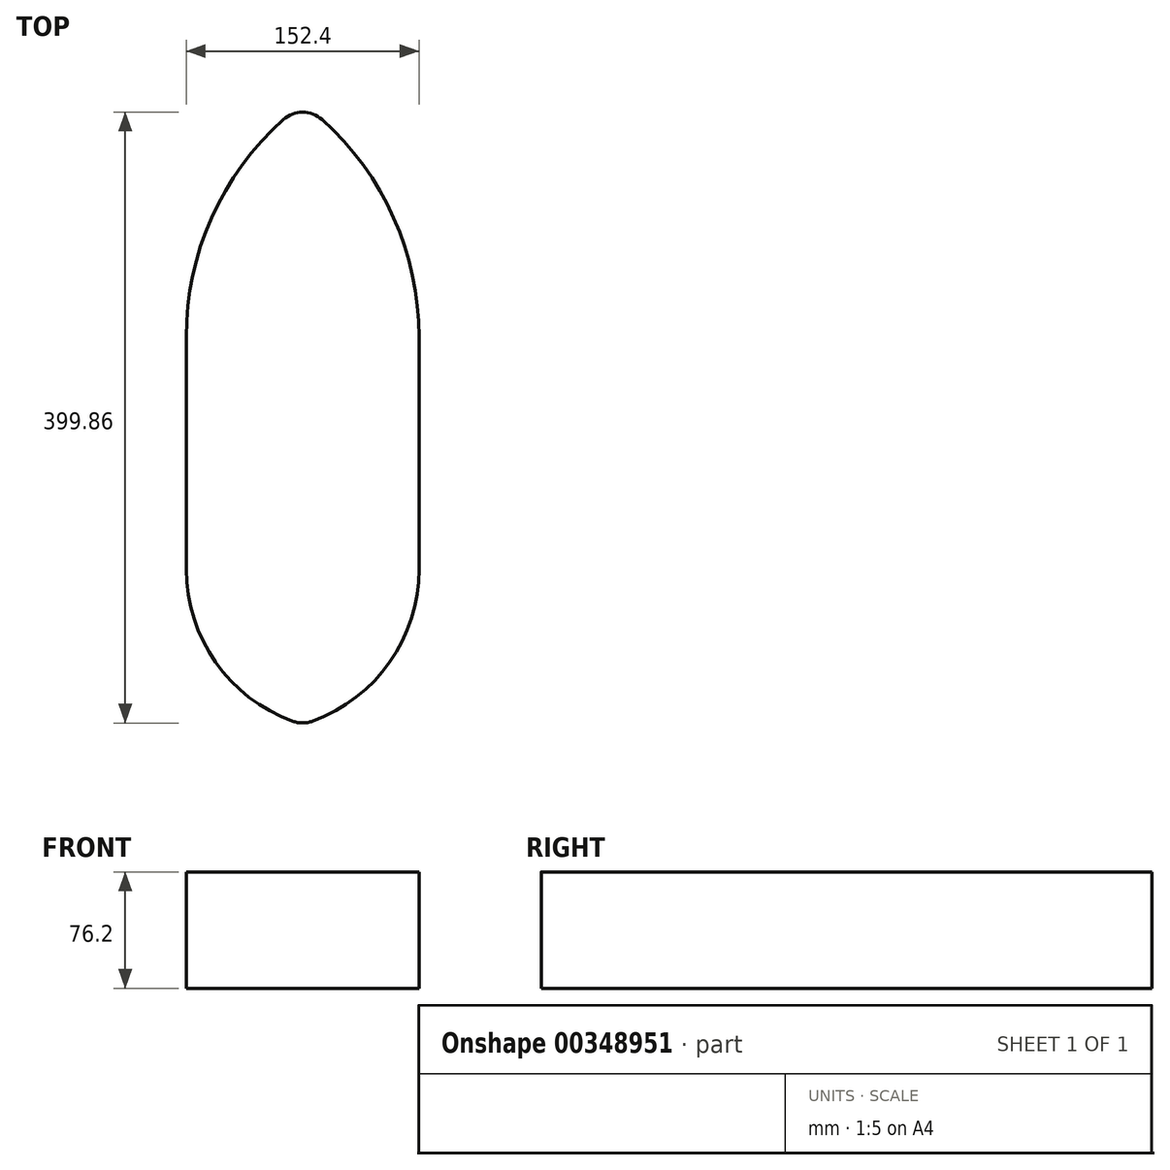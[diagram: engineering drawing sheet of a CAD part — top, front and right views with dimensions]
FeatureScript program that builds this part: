
annotation { "Feature Type Name" : "Feature", "Feature Type Description" : "" }
export const myFeature = defineFeature(function(context is Context, id is Id, definition is map)
    precondition{}
    {
        {
            var Q0;
            Q0=qCreatedBy(makeId("Top.planeOp"),FACE);
            var sketch = newSketch(context, id + "F0", { "sketchPlane" : qUnion([Q0])});
            skLineSegment(sketch, "E0", {"start": v(0, 0) * mm, "end": v(-76.2, 0) * mm, "construction": true});
            skLineSegment(sketch, "E1", {"start": v(0, 0) * mm, "end": v(76.2, 0) * mm, "construction": true});
            skLineSegment(sketch, "E2", {"start": v(-76.2, 76.2) * mm, "end": v(-76.2, -76.2) * mm});
            skLineSegment(sketch, "E3", {"start": v(76.2, 76.2) * mm, "end": v(76.2, -76.2) * mm});
            skLineSegment(sketch, "E4", {"start": v(-76.2, -76.2) * mm, "end": v(0, -76.2) * mm, "construction": true});
            skLineSegment(sketch, "E5", {"start": v(0, -76.2) * mm, "end": v(76.2, -76.2) * mm, "construction": true});
            skLineSegment(sketch, "E6", {"start": v(0, 76.2) * mm, "end": v(-76.2, 76.2) * mm, "construction": true});
            skLineSegment(sketch, "E7", {"start": v(0, 76.2) * mm, "end": v(76.2, 76.2) * mm, "construction": true});
            skLineSegment(sketch, "E8", {"start": v(0, 76.2) * mm, "end": v(0, -76.2) * mm, "construction": true});
            skLineSegment(sketch, "E9", {"start": v(0, -76.2) * mm, "end": v(0, -177.8) * mm, "construction": true});
            skArc(sketch, "E10", {"start": v(-76.2, -76.2) * mm, "mid": v(-57.04, -136.93) * mm, "end": v(-6.5, -175.67) * mm});
            skArc(sketch, "E11.MirrorCS", {"start": v(76.2, -76.2) * mm, "mid": v(57.04, -136.93) * mm, "end": v(6.5, -175.67) * mm});
            skPoint(sketch, "E12.visualSharp", {"position": v(0, -177.8) * mm});
            skArc(sketch, "E12.filletArc", {"start": v(-6.5, -175.67) * mm, "mid": v(0, -176.82) * mm, "end": v(6.5, -175.67) * mm});
            skLineSegment(sketch, "E13", {"start": v(0, 76.2) * mm, "end": v(0, 228.6) * mm, "construction": true});
            skArc(sketch, "E14", {"start": v(-12.7, 218.2) * mm, "mid": v(-59.6, 153.97) * mm, "end": v(-76.2, 76.2) * mm});
            skArc(sketch, "E15.MirrorCS", {"start": v(12.7, 218.2) * mm, "mid": v(59.6, 153.97) * mm, "end": v(76.2, 76.2) * mm});
            skPoint(sketch, "E16.visualSharp", {"position": v(0, 228.6) * mm});
            skArc(sketch, "E16.filletArc", {"start": v(12.7, 218.2) * mm, "mid": v(0, 223.04) * mm, "end": v(-12.7, 218.2) * mm});
            skLineSegment(sketch, "E17", {"start": v(0, 185.63) * mm, "end": v(76.2, 185.63) * mm, "construction": true});
            skLineSegment(sketch, "E18", {"start": v(12.7, 218.2) * mm, "end": v(12.7, 185.63) * mm, "construction": true});
            skLineSegment(sketch, "E19", {"start": v(12.7, 185.63) * mm, "end": v(12.7, 76.2) * mm, "construction": true});
            skLineSegment(sketch, "E20.MirrorCS", {"start": v(0, 185.63) * mm, "end": v(-76.2, 185.63) * mm, "construction": true});
            skLineSegment(sketch, "E21.MirrorCS", {"start": v(-12.7, 185.63) * mm, "end": v(-12.7, 76.2) * mm, "construction": true});
            skLineSegment(sketch, "E22.MirrorCS", {"start": v(-12.7, 218.2) * mm, "end": v(-12.7, 185.63) * mm, "construction": true});
            skArc(sketch, "E23", {"start": v(69.4, 180.76) * mm, "mid": v(61.51, 170.86) * mm, "end": v(57.3, 158.92) * mm});
            skLineSegment(sketch, "E24", {"start": v(82.12, 185.63) * mm, "end": v(222.66, 185.63) * mm});
            skArc(sketch, "E25", {"start": v(152.22, 152.4) * mm, "mid": v(98.45, 130.02) * mm, "end": v(76.2, 76.2) * mm});
            skLineSegment(sketch, "E26", {"start": v(152.25, 152.4) * mm, "end": v(203.2, 152.4) * mm});
            skPoint(sketch, "E27.visualSharp", {"position": v(76.2, 185.63) * mm});
            skArc(sketch, "E27.filletArc", {"start": v(82.12, 185.63) * mm, "mid": v(75.3, 184.37) * mm, "end": v(69.4, 180.76) * mm});
            skPoint(sketch, "E28.visualSharp", {"position": v(152.57, 152.4) * mm});
            skArc(sketch, "E28.filletArc", {"start": v(152.25, 152.4) * mm, "mid": v(152.23, 152.4) * mm, "end": v(152.22, 152.4) * mm});
            skCircle(sketch, "E29", {"center": v(241.3, 152.4) * mm, "radius": 38.1 * mm});
            skLineSegment(sketch, "E30", {"start": v(203.2, 152.4) * mm, "end": v(203.2, 0) * mm, "construction": true});
            skLineSegment(sketch, "E31", {"start": v(203.2, 0) * mm, "end": v(76.2, 0) * mm, "construction": true});
            skLineSegment(sketch, "E32", {"start": v(76.2, 76.2) * mm, "end": v(203.2, 76.2) * mm, "construction": true});
            skLineSegment(sketch, "E33", {"start": v(152.57, 152.4) * mm, "end": v(60.2, 152.6) * mm, "construction": true});
            skLineSegment(sketch, "E34", {"start": v(241.3, 152.4) * mm, "end": v(203.2, 152.4) * mm, "construction": true});
            skArc(sketch, "E35.MirrorCS", {"start": v(-152.22, 152.4) * mm, "mid": v(-98.45, 130.02) * mm, "end": v(-76.2, 76.2) * mm});
            skLineSegment(sketch, "E36.MirrorCS", {"start": v(-152.57, 152.4) * mm, "end": v(-60.2, 152.6) * mm, "construction": true});
            skLineSegment(sketch, "E37.MirrorCS", {"start": v(-152.25, 152.4) * mm, "end": v(-203.2, 152.4) * mm});
            skLineSegment(sketch, "E38.MirrorCS", {"start": v(-241.3, 152.4) * mm, "end": v(-203.2, 152.4) * mm, "construction": true});
            skCircle(sketch, "E39.MirrorC", {"center": v(-241.3, 152.4) * mm, "radius": 38.1 * mm});
            skLineSegment(sketch, "E40.MirrorCS", {"start": v(-82.12, 185.63) * mm, "end": v(-222.66, 185.63) * mm});
            skArc(sketch, "E41.MirrorCS", {"start": v(-82.12, 185.63) * mm, "mid": v(-75.3, 184.37) * mm, "end": v(-69.4, 180.76) * mm});
            skArc(sketch, "E42.MirrorCS", {"start": v(-69.4, 180.76) * mm, "mid": v(-61.51, 170.86) * mm, "end": v(-57.3, 158.92) * mm});
            skArc(sketch, "E43.MirrorCS", {"start": v(152.22, -152.4) * mm, "mid": v(98.45, -130.02) * mm, "end": v(76.2, -76.2) * mm});
            skLineSegment(sketch, "E44.MirrorCS", {"start": v(152.25, -152.4) * mm, "end": v(203.2, -152.4) * mm});
            skLineSegment(sketch, "E45.MirrorCS", {"start": v(82.12, -185.63) * mm, "end": v(222.66, -185.63) * mm});
            skCircle(sketch, "E46.MirrorC", {"center": v(241.3, -152.4) * mm, "radius": 38.1 * mm});
            skLineSegment(sketch, "E47.MirrorCS", {"start": v(241.3, -152.4) * mm, "end": v(203.2, -152.4) * mm, "construction": true});
            skArc(sketch, "E48.MirrorCS", {"start": v(82.12, -185.63) * mm, "mid": v(75.3, -184.37) * mm, "end": v(69.4, -180.76) * mm});
            skArc(sketch, "E49", {"start": v(57.04, -136.93) * mm, "mid": v(57.9, -160.34) * mm, "end": v(69.4, -180.76) * mm});
            skArc(sketch, "E50.MirrorCS", {"start": v(-57.04, -136.93) * mm, "mid": v(-57.9, -160.34) * mm, "end": v(-69.4, -180.76) * mm});
            skArc(sketch, "E51.MirrorCS", {"start": v(-82.12, -185.63) * mm, "mid": v(-75.3, -184.37) * mm, "end": v(-69.4, -180.76) * mm});
            skLineSegment(sketch, "E52.MirrorCS", {"start": v(-82.12, -185.63) * mm, "end": v(-222.66, -185.63) * mm});
            skCircle(sketch, "E53.MirrorC", {"center": v(-241.3, -152.4) * mm, "radius": 38.1 * mm});
            skLineSegment(sketch, "E54.MirrorCS", {"start": v(-241.3, -152.4) * mm, "end": v(-203.2, -152.4) * mm, "construction": true});
            skLineSegment(sketch, "E55.MirrorCS", {"start": v(-152.25, -152.4) * mm, "end": v(-203.2, -152.4) * mm});
            skArc(sketch, "E56", {"start": v(-152.25, -152.4) * mm, "mid": v(-98.42, -130.07) * mm, "end": v(-76.2, -76.2) * mm});
            skArc(sketch, "E57", {"start": v(-203.2, 152.4) * mm, "mid": v(-208.42, 171.65) * mm, "end": v(-222.66, 185.63) * mm});
            skSolve(sketch);
        }
        {
            var Q0;
            {var subQ12=sQuery(id+"F0.wireOp",EDGE,"E2");Q0=makeQuery(id+"F0.imprint","IMPRINT",FACE,{"disambiguationData":[TD([[makeQuery(id+"F0.imprint","IMPRINT",EDGE,{"derivedFrom":subQ12}),1.0]])]});}
            extrude(context, id + "F1", {"entities" : qUnion([Q0]), "endBound" : BoundingType.SYMMETRIC, "depth" : 76.2 * mm});
        }
    });
